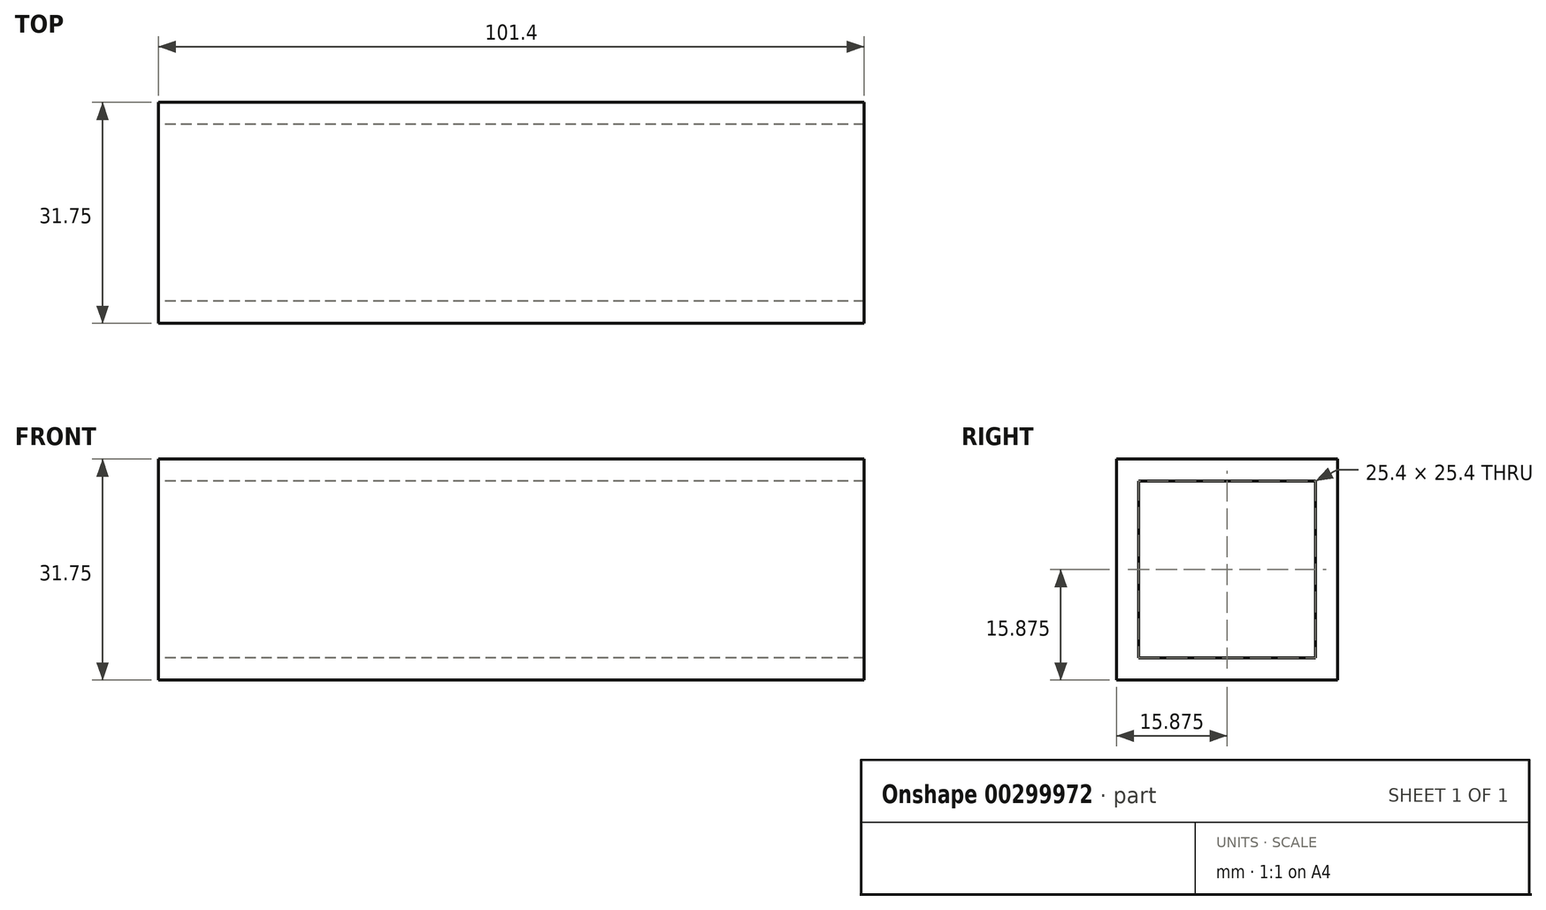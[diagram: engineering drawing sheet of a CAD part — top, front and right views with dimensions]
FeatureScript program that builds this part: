
annotation { "Feature Type Name" : "Feature", "Feature Type Description" : "" }
export const myFeature = defineFeature(function(context is Context, id is Id, definition is map)
    precondition{}
    {
        {
            var Q0;
            Q0=qCreatedBy(makeId("Right.planeOp"),FACE);
            var sketch = newSketch(context, id + "F0", { "sketchPlane" : qUnion([Q0])});
            skLineSegment(sketch, "E0.bottom", {"start": v(0, 0) * mm, "end": v(31.75, 0) * mm});
            skLineSegment(sketch, "E0.top", {"start": v(0, 31.75) * mm, "end": v(31.75, 31.75) * mm});
            skLineSegment(sketch, "E0.left", {"start": v(0, 0) * mm, "end": v(0, 31.75) * mm});
            skLineSegment(sketch, "E0.right", {"start": v(31.75, 0) * mm, "end": v(31.75, 31.75) * mm});
            skLineSegment(sketch, "E1.bottom", {"start": v(3.17, 28.57) * mm, "end": v(28.57, 28.57) * mm});
            skLineSegment(sketch, "E1.top", {"start": v(3.17, 3.17) * mm, "end": v(28.57, 3.17) * mm});
            skLineSegment(sketch, "E1.left", {"start": v(3.17, 28.57) * mm, "end": v(3.18, 3.17) * mm});
            skLineSegment(sketch, "E1.right", {"start": v(28.57, 28.57) * mm, "end": v(28.58, 3.17) * mm});
            skSolve(sketch);
        }
        {
            var Q0;
            Q0=qSketchRegion(id+"F0",true);
            extrude(context, id + "F1", {"entities" : qUnion([Q0]), "depth" : 101.4 * mm, "offsetDistance" : 25 * mm});
        }
    });
